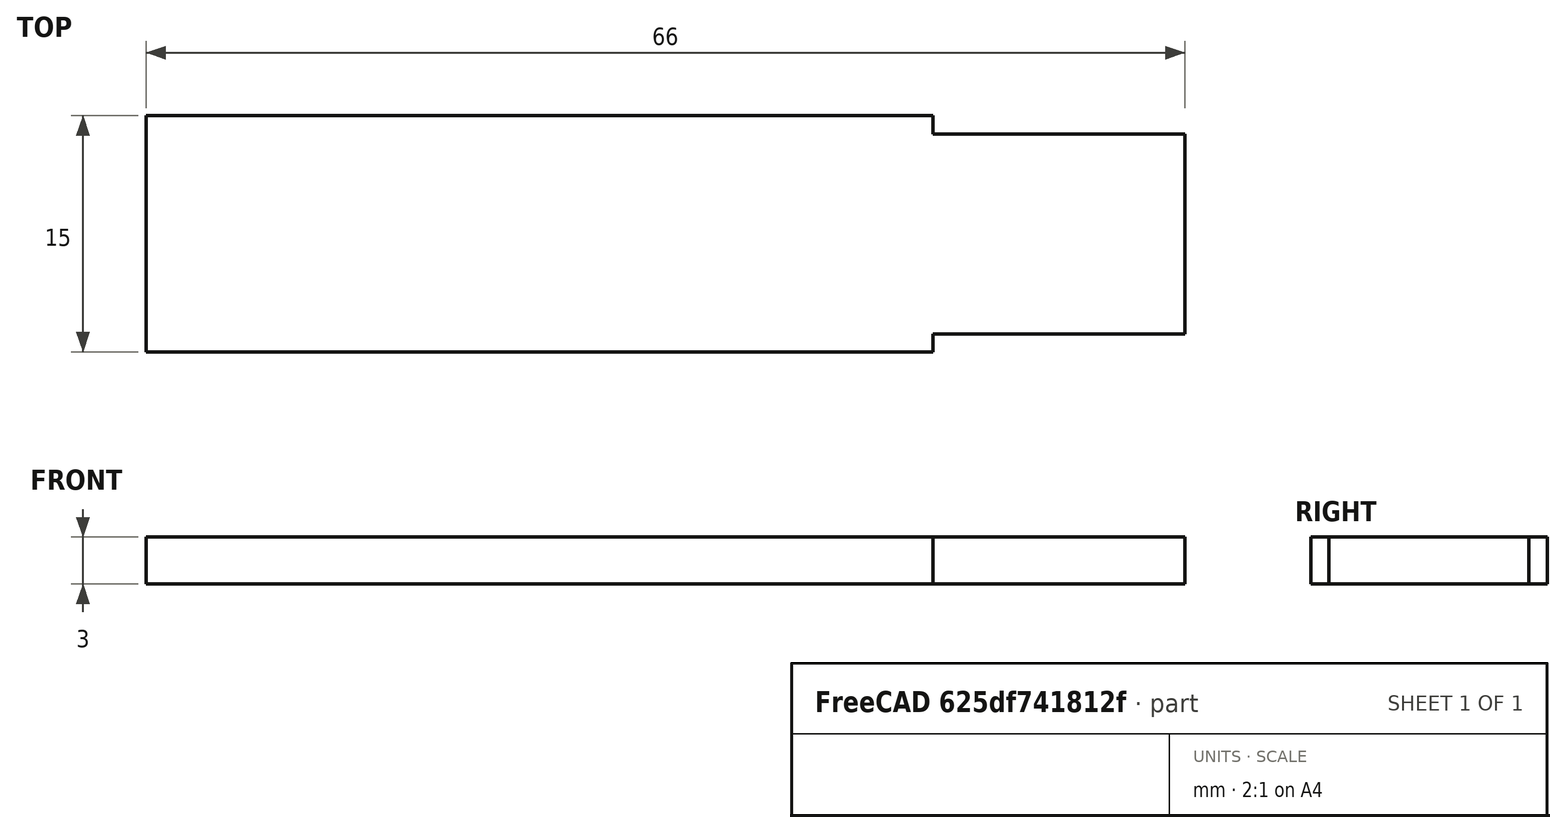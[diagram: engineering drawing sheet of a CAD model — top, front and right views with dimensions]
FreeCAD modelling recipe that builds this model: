
FCSTD DOCUMENT  (FreeCAD 0.16R)
Label: Wobble_shaft
License: All rights reserved
LicenseURL: http://en.wikipedia.org/wiki/All_rights_reserved
objects: Sketcher::SketchObject×1, PartDesign::Pad×1, Mesh::Feature×1
note: 3 computed .brp shape members not serialized (recipe doc carries the construction recipe); baked Part::Feature solids carry a one-line shape summary decoded from their .brp

FEATURE [Sketcher::SketchObject] Sketch
  sketch-geometry (8):
    g0: LineSegment StartX=-66 StartY=7.5 StartZ=0 EndX=-16 EndY=7.5 EndZ=0
    g1: LineSegment StartX=-16 StartY=7.5 StartZ=0 EndX=-16 EndY=6.35 EndZ=0
    g2: LineSegment StartX=-16 StartY=6.35 StartZ=0 EndX=0 EndY=6.35 EndZ=0
    g3: LineSegment StartX=0 StartY=6.35 StartZ=0 EndX=0 EndY=-6.35 EndZ=0
    g4: LineSegment StartX=0 StartY=-6.35 StartZ=0 EndX=-16 EndY=-6.35 EndZ=0
    g5: LineSegment StartX=-16 StartY=-6.35 StartZ=0 EndX=-16 EndY=-7.5 EndZ=0
    g6: LineSegment StartX=-16 StartY=-7.5 StartZ=0 EndX=-66 EndY=-7.5 EndZ=0
    g7: LineSegment StartX=-66 StartY=-7.5 StartZ=0 EndX=-66 EndY=7.5 EndZ=0
  constraints (23):
    c: Horizontal(g0)
    c: Coincident(g0,g1)
    c: Coincident(g1,g2)
    c: Horizontal(g2)
    c: Coincident(g2,g3)
    c: Coincident(g3,g4)
    c: Horizontal(g4)
    c: Coincident(g4,g5)
    c: Coincident(g5,g6)
    c: Coincident(g6,g7)
    c: Coincident(g7,g0)
    c: Vertical(g7)
    c: Vertical(g1)
    c: Vertical(g5)
    c: Symmetric(g4,g1,g-1)
    c: Symmetric(g2,g3,g-1)
    c: Symmetric(g6,g0,g-1)
    c: Symmetric(g5,g0,g-1)
    c: Distance(g3) = 12.7
    c: Distance(g5,g0) = 15
    c: Distance(g2) = 16
    c: Distance(g6) = 50
    c: PointOnObject(g3,g-2)
FEATURE [PartDesign::Pad] Pad
  Length = 3
  Length2 = 100
  Sketch = -> Sketch
  Type = 0
FEATURE [Mesh::Feature] Mesh  label="Pad (Meshed)"
